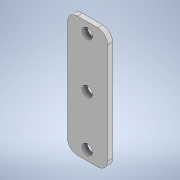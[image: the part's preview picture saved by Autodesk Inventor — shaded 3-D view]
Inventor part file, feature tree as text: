
AUTODESK INVENTOR PART (.ipt)
format: ipt  version: 2022 (Build 260153000, 153)  size: 121,344 bytes
history: native  units: mm
features: extrude x2, sketch x2
ambient origin geometry x8: Origin, YZ Plane, XZ Plane, XY Plane, X Axis, Y Axis, Z Axis, Center Point
bodies: Solid1 (feature_tree)
feature tree (4):
  extrude  "Extrusion1"  Depth=40.0mm
  extrude  "Extrusion2"  Depth=5.0mm TaperAngle=0.0deg
  sketch  "Sketch1"  dims[d0=10.0mm d1=40.0mm]
  sketch  "Sketch2"  dims[d2=120.0mm d3=5.0mm d4=0.0mm d5=10.0mm d7=10.0mm d8=10.0mm d9=5.0mm d10=0.0mm]
